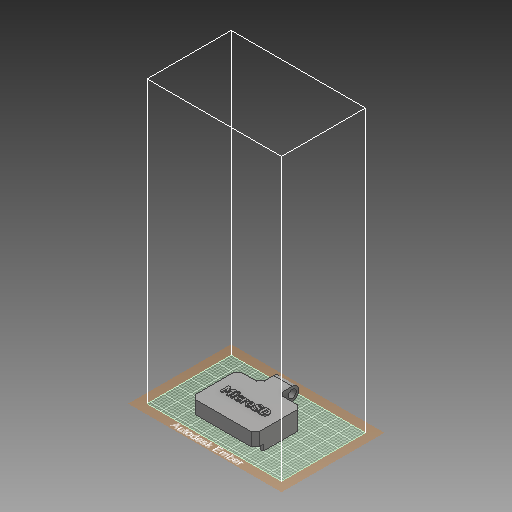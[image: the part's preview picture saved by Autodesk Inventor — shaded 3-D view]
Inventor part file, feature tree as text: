
AUTODESK INVENTOR PART (.ipt)
format: ipt  version: 2018 (Build 220112000, 112)  size: 554,496 bytes
history: native  units: in
note: dims shown in document units (in); Inventor stores cm internally (conversion verified against a paired STEP export)
features: extrude x3, sketch x3, fillet x1, chamfer x1
ambient origin geometry x8: Origin, YZ Plane, XZ Plane, XY Plane, X Axis, Y Axis, Z Axis, Center Point
bodies: Solid1 (feature_tree)
feature tree (8):
  extrude  "Extrusion1"  Depth=0.375in
  extrude  "Extrusion2"  Depth=0.425in
  fillet  "Fillet1"  Radius=0.246in
  chamfer  "Chamfer1"  Distance=0.123in
  extrude  "Extrusion3"  Depth=0.246in TaperAngle=0.0deg
  sketch  "Sketch1"  dims[d0=0.425in d1=0.375in]
  sketch  "Sketch2"  dims[d2=0.35in d3=0.425in d5=0.246in d6=0.0in]
  sketch  "Sketch4"  dims[d7=0.146in d8=0.123in d9=0.246in d10=0.0in d11=0.123in d12=0.075in d13=0.125in d14=45.0deg d17=1.246in d18=0.05in d19=0.125in d22=0.11in d23=0.0in]
